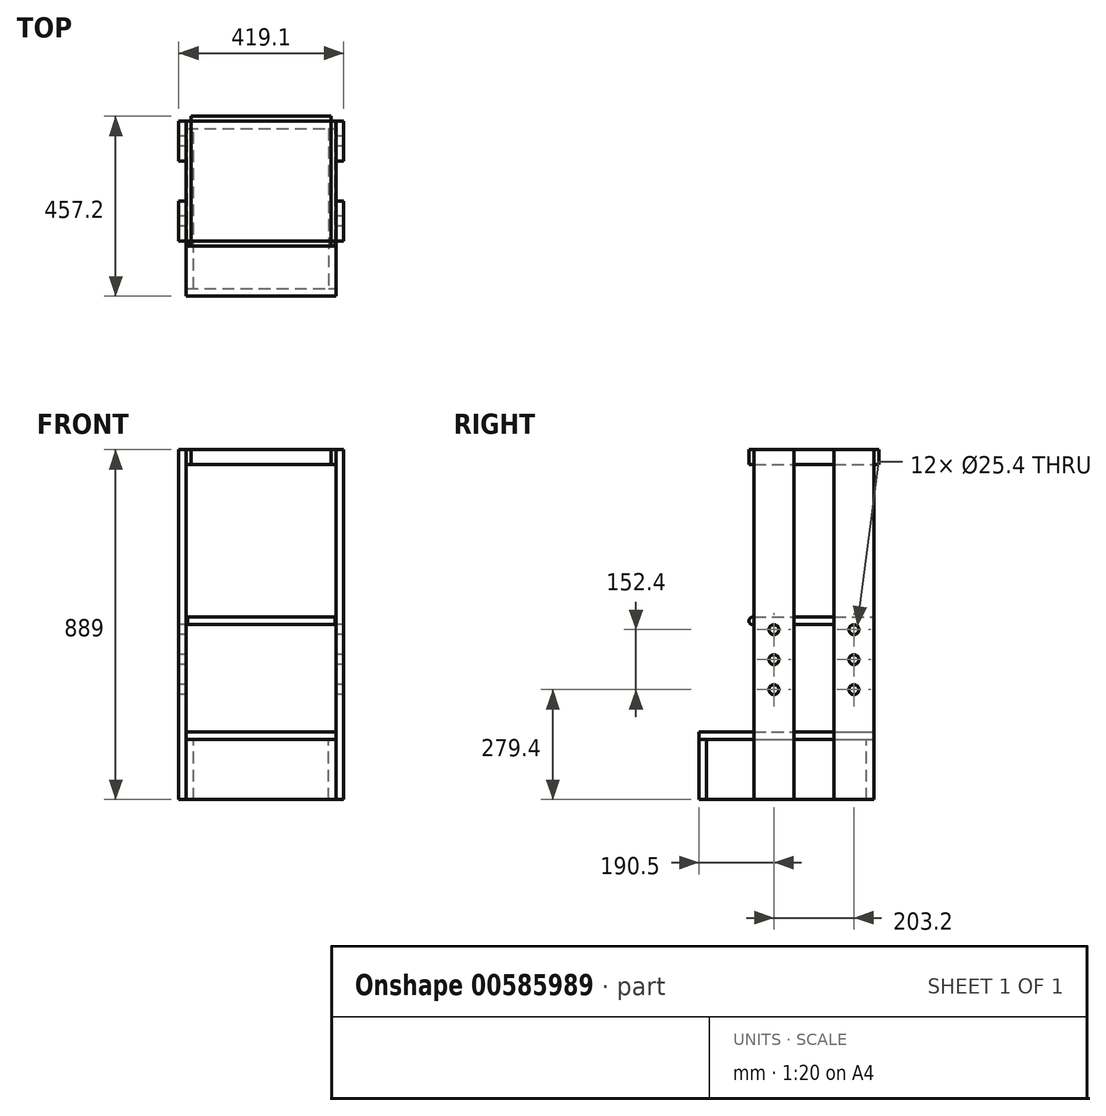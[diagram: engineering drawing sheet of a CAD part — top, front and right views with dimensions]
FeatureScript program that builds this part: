
annotation { "Feature Type Name" : "Feature", "Feature Type Description" : "" }
export const myFeature = defineFeature(function(context is Context, id is Id, definition is map)
    precondition{}
    {
        {
            var Q0;
            Q0=qCreatedBy(makeId("Top.planeOp"),FACE);
            var sketch = newSketch(context, id + "F0", { "sketchPlane" : qUnion([Q0])});
            skLineSegment(sketch, "E0.bottom", {"start": v(190.5, -222.25) * mm, "end": v(-190.5, -222.25) * mm});
            skLineSegment(sketch, "E0.top", {"start": v(190.5, 222.25) * mm, "end": v(-190.5, 222.25) * mm});
            skLineSegment(sketch, "E0.left", {"start": v(190.5, -222.25) * mm, "end": v(190.5, 222.25) * mm});
            skLineSegment(sketch, "E0.right", {"start": v(-190.5, -222.25) * mm, "end": v(-190.5, 222.25) * mm});
            skPoint(sketch, "E0.middle", {"position": v(0, 0) * mm});
            skSolve(sketch);
        }
        {
            var Q0;
            Q0=makeQuery(id+"F0.imprint","IMPRINT",FACE,{"disambiguationData":[TD([[makeQuery(id+"F0.imprint","IMPRINT",EDGE,{"derivedFrom":sQuery(id+"F0.wireOp",EDGE,"E0.bottom")}),-1.0]])]});
            var Q1;
            Q1=sQuery(id+"F0.wireOp",EDGE,"E0.right");
            extrude(context, id + "F1", {"entities" : qUnion([Q0]), "surfaceEntities" : qUnion([Q1]), "depth" : 19.05 * mm, "offsetDistance" : 25.4 * mm});
        }
        {
            var Q0;
            Q0=makeQuery(id+"F0.imprint","IMPRINT",FACE,{"disambiguationData":[TD([[makeQuery(id+"F0.imprint","IMPRINT",EDGE,{"derivedFrom":sQuery(id+"F0.wireOp",EDGE,"E0.bottom")}),-1.0]])]});
            var sketch = newSketch(context, id + "F2", { "sketchPlane" : qUnion([Q0])});
            skLineSegment(sketch, "E1.bottom", {"start": v(-190.5, 222.25) * mm, "end": v(190.5, 222.25) * mm});
            skLineSegment(sketch, "E1.top", {"start": v(-190.5, 203.2) * mm, "end": v(190.5, 203.2) * mm});
            skLineSegment(sketch, "E1.left", {"start": v(-190.5, 222.25) * mm, "end": v(-190.5, 203.2) * mm});
            skLineSegment(sketch, "E1.right", {"start": v(190.5, 222.25) * mm, "end": v(190.5, 203.2) * mm});
            skLineSegment(sketch, "E2.bottom", {"start": v(-190.5, -222.25) * mm, "end": v(190.5, -222.25) * mm});
            skLineSegment(sketch, "E2.top", {"start": v(-190.5, -203.2) * mm, "end": v(190.5, -203.2) * mm});
            skLineSegment(sketch, "E2.left", {"start": v(-190.5, -222.25) * mm, "end": v(-190.5, -203.2) * mm});
            skLineSegment(sketch, "E2.right", {"start": v(190.5, -222.25) * mm, "end": v(190.5, -203.2) * mm});
            skSolve(sketch);
        }
        {
            var Q0;
            Q0=makeQuery(id+"F2.imprint","IMPRINT",FACE,{"disambiguationData":[TD([[makeQuery(id+"F2.imprint","IMPRINT",EDGE,{"derivedFrom":sQuery(id+"F2.wireOp",EDGE,"E1.bottom")}),1.0]])]});
            var Q1;
            Q1=makeQuery(id+"F2.imprint","IMPRINT",FACE,{"disambiguationData":[TD([[makeQuery(id+"F2.imprint","IMPRINT",EDGE,{"derivedFrom":sQuery(id+"F2.wireOp",EDGE,"E2.bottom")}),-1.0]])]});
            extrude(context, id + "F3", {"entities" : qUnion([Q0, Q1]), "oppositeDirection" : true, "depth" : 152.4 * mm, "offsetDistance" : 25.4 * mm});
        }
        {
            var Q0;
            Q0=makeQuery(id+"F0.imprint","IMPRINT",FACE,{"disambiguationData":[TD([[makeQuery(id+"F0.imprint","IMPRINT",EDGE,{"derivedFrom":sQuery(id+"F0.wireOp",EDGE,"E0.bottom")}),-1.0]])]});
            var sketch = newSketch(context, id + "F4", { "sketchPlane" : qUnion([Q0])});
            skLineSegment(sketch, "E3.bottom", {"start": v(-190.5, -203.2) * mm, "end": v(-171.45, -203.2) * mm});
            skLineSegment(sketch, "E3.top", {"start": v(-190.5, 203.2) * mm, "end": v(-171.45, 203.2) * mm});
            skLineSegment(sketch, "E3.left", {"start": v(-190.5, -203.2) * mm, "end": v(-190.5, 203.2) * mm});
            skLineSegment(sketch, "E3.right", {"start": v(-171.45, -203.2) * mm, "end": v(-171.45, 203.2) * mm});
            skLineSegment(sketch, "E4.bottom", {"start": v(171.45, 203.2) * mm, "end": v(190.5, 203.2) * mm});
            skLineSegment(sketch, "E4.top", {"start": v(171.45, -203.2) * mm, "end": v(190.5, -203.2) * mm});
            skLineSegment(sketch, "E4.left", {"start": v(171.45, 203.2) * mm, "end": v(171.45, -203.2) * mm});
            skLineSegment(sketch, "E4.right", {"start": v(190.5, 203.2) * mm, "end": v(190.5, -203.2) * mm});
            skSolve(sketch);
        }
        {
            var Q0;
            Q0 = qSketchRegion(id + "F4", true);
            extrude(context, id + "F5", {"entities" : qUnion([Q0]), "oppositeDirection" : true, "depth" : 152.4 * mm, "offsetDistance" : 25.4 * mm});
        }
        {
            var Q0;
            Q0=makeQuery(id+"F5.opExtrude","SWEPT_FACE",FACE,{"disambiguationData":[OSD([sQuery(id+"F4.wireOp",EDGE,"E3.left")])]});
            var sketch = newSketch(context, id + "F6", { "sketchPlane" : qUnion([Q0])});
            skLineSegment(sketch, "E5.bottom", {"start": v(-222.25, -152.4) * mm, "end": v(-120.65, -152.4) * mm});
            skLineSegment(sketch, "E5.top", {"start": v(-222.25, 736.6) * mm, "end": v(-120.65, 736.6) * mm});
            skLineSegment(sketch, "E5.left", {"start": v(-222.25, -152.4) * mm, "end": v(-222.25, 736.6) * mm});
            skLineSegment(sketch, "E5.right", {"start": v(-120.65, -152.4) * mm, "end": v(-120.65, 736.6) * mm});
            skLineSegment(sketch, "E6.bottom", {"start": v(-19.05, -152.4) * mm, "end": v(82.55, -152.4) * mm});
            skLineSegment(sketch, "E6.top", {"start": v(-19.05, 736.6) * mm, "end": v(82.55, 736.6) * mm});
            skLineSegment(sketch, "E6.left", {"start": v(-19.05, -152.4) * mm, "end": v(-19.05, 736.6) * mm});
            skLineSegment(sketch, "E6.right", {"start": v(82.55, -152.4) * mm, "end": v(82.55, 736.6) * mm});
            skSolve(sketch);
        }
        {
            var Q0;
            Q0 = qSketchRegion(id + "F6", true);
            extrude(context, id + "F7", {"entities" : qUnion([Q0]), "depth" : 19.05 * mm, "offsetDistance" : 25.4 * mm});
        }
        {
            var Q0;
            Q0=makeQuery(id+"F7.opExtrude","SWEPT_BODY",BODY,{"disambiguationData":[OSD([sQuery(id+"F6.wireOp",EDGE,"E6.bottom"),sQuery(id+"F6.wireOp",EDGE,"E6.top"),sQuery(id+"F6.wireOp",EDGE,"E6.left"),sQuery(id+"F6.wireOp",EDGE,"E6.right")])]});
            var Q1;
            Q1=makeQuery(id+"F7.opExtrude","SWEPT_BODY",BODY,{"disambiguationData":[OSD([sQuery(id+"F6.wireOp",EDGE,"E5.bottom"),sQuery(id+"F6.wireOp",EDGE,"E5.top"),sQuery(id+"F6.wireOp",EDGE,"E5.left"),sQuery(id+"F6.wireOp",EDGE,"E5.right")])]});
            var Q2;
            Q2=qCreatedBy(makeId("Right.planeOp"),FACE);
            mirror(context, id + "F8", {"entities" : qUnion([Q0, Q1]), "mirrorPlane" : qUnion([Q2])});
        }
        {
            var Q0;
            Q0=makeQuery(id+"F7.opExtrude","CAP_FACE",FACE,{"disambiguationData":[OSD([sQuery(id+"F6.wireOp",EDGE,"E5.bottom"),sQuery(id+"F6.wireOp",EDGE,"E5.top"),sQuery(id+"F6.wireOp",EDGE,"E5.left"),sQuery(id+"F6.wireOp",EDGE,"E5.right")])],"isStart":false});
            var sketch = newSketch(context, id + "F9", { "sketchPlane" : qUnion([Q0])});
            skLineSegment(sketch, "E7", {"start": v(-171.45, 736.6) * mm, "end": v(-171.45, -152.4) * mm, "construction": true});
            skLineSegment(sketch, "E8", {"start": v(31.75, 736.6) * mm, "end": v(31.75, -152.4) * mm, "construction": true});
            skCircle(sketch, "E9", {"center": v(-171.45, 279.4) * mm, "radius": 12.7 * mm});
            skCircle(sketch, "E10", {"center": v(-171.45, 203.2) * mm, "radius": 12.7 * mm});
            skCircle(sketch, "E11", {"center": v(-171.45, 127) * mm, "radius": 12.7 * mm});
            skCircle(sketch, "E12", {"center": v(31.75, 127) * mm, "radius": 12.7 * mm});
            skCircle(sketch, "E13", {"center": v(31.75, 203.2) * mm, "radius": 12.7 * mm});
            skCircle(sketch, "E14", {"center": v(31.75, 279.4) * mm, "radius": 12.7 * mm});
            skLineSegment(sketch, "E15", {"start": v(-171.45, 292.1) * mm, "end": v(31.75, 292.1) * mm, "construction": true});
            skLineSegment(sketch, "E16", {"start": v(31.75, 292.1) * mm, "end": v(31.75, 215.9) * mm, "construction": true});
            skLineSegment(sketch, "E17", {"start": v(31.75, 215.9) * mm, "end": v(-171.45, 215.9) * mm, "construction": true});
            skLineSegment(sketch, "E18", {"start": v(-171.45, 215.9) * mm, "end": v(-171.45, 139.7) * mm, "construction": true});
            skLineSegment(sketch, "E19", {"start": v(-171.45, 139.7) * mm, "end": v(31.75, 139.7) * mm, "construction": true});
            skSolve(sketch);
        }
        {
            var Q0;
            Q0=sQuery(id+"F9.wireOp",VERTEX,"E9.center");
            var Q1;
            Q1=sQuery(id+"F9.wireOp",VERTEX,"E14.center");
            var Q2;
            Q2=sQuery(id+"F9.wireOp",VERTEX,"E13.center");
            var Q3;
            Q3=sQuery(id+"F9.wireOp",VERTEX,"E10.center");
            var Q4;
            Q4=sQuery(id+"F9.wireOp",VERTEX,"E11.center");
            var Q5;
            Q5=sQuery(id+"F9.wireOp",VERTEX,"E12.center");
            var Q6;
            Q6=makeQuery(id+"F7.opExtrude","SWEPT_BODY",BODY,{"disambiguationData":[OSD([sQuery(id+"F6.wireOp",EDGE,"E6.bottom"),sQuery(id+"F6.wireOp",EDGE,"E6.top"),sQuery(id+"F6.wireOp",EDGE,"E6.left"),sQuery(id+"F6.wireOp",EDGE,"E6.right")])]});
            var Q7;
            Q7=makeQuery(id+"F7.opExtrude","SWEPT_BODY",BODY,{"disambiguationData":[OSD([sQuery(id+"F6.wireOp",EDGE,"E5.bottom"),sQuery(id+"F6.wireOp",EDGE,"E5.top"),sQuery(id+"F6.wireOp",EDGE,"E5.left"),sQuery(id+"F6.wireOp",EDGE,"E5.right")])]});
            var Q8;
            Q8=makeQuery(id+"F8.opPattern","COPY",BODY,{"derivedFrom":makeQuery(id+"F7.opExtrude","SWEPT_BODY",BODY,{"disambiguationData":[OSD([sQuery(id+"F6.wireOp",EDGE,"E5.bottom"),sQuery(id+"F6.wireOp",EDGE,"E5.top"),sQuery(id+"F6.wireOp",EDGE,"E5.left"),sQuery(id+"F6.wireOp",EDGE,"E5.right")])]}),"instanceName":"1"});
            var Q9;
            Q9=makeQuery(id+"F8.opPattern","COPY",BODY,{"derivedFrom":makeQuery(id+"F7.opExtrude","SWEPT_BODY",BODY,{"disambiguationData":[OSD([sQuery(id+"F6.wireOp",EDGE,"E6.bottom"),sQuery(id+"F6.wireOp",EDGE,"E6.top"),sQuery(id+"F6.wireOp",EDGE,"E6.left"),sQuery(id+"F6.wireOp",EDGE,"E6.right")])]}),"instanceName":"1"});
            hole(context, id + "F10", {"style" : HoleStyle.SIMPLE, "endStyle" : HoleEndStyle.THROUGH, "holeDiameter" : 25.4 * mm, "majorDiameter" : 6.35 * mm, "isTappedThrough" : true, "tappedDepth" : 12.7 * mm, "tapClearance" : 3, "locations" : qUnion([Q0, Q1, Q2, Q3, Q4, Q5]), "scope" : qUnion([Q6, Q7, Q8, Q9])});
        }
        {
            var Q0;
            Q0=sQuery(id+"F9.wireOp",EDGE,"E15");
            cPoint(context, id + "F11", {"entities" : qUnion([Q0]), "parameter" : 0.5});
        }
        {
            var Q0;
            Q0 = qCreatedBy(id + "F11" ,VERTEX);
            var Q1;
            Q1=qCreatedBy(makeId("Top.planeOp"),FACE);
            cPlane(context, id + "F12", {"entities" : qUnion([Q0, Q1]), "cplaneType" : CPlaneType.PLANE_POINT, "offset" : 304.8 * mm, "width" : 152.4 * mm, "height" : 152.4 * mm});
        }
        {
            var Q0;
            Q0=qCreatedBy(id+"F12.planeOp",FACE);
            var sketch = newSketch(context, id + "F13", { "sketchPlane" : qUnion([Q0])});
            skLineSegment(sketch, "E20.bottom", {"start": v(187.32, -95.25) * mm, "end": v(-187.32, -95.25) * mm});
            skLineSegment(sketch, "E20.top", {"start": v(187.33, 222.25) * mm, "end": v(-187.33, 222.25) * mm});
            skLineSegment(sketch, "E20.left", {"start": v(187.33, -26.1) * mm, "end": v(187.33, 222.25) * mm});
            skLineSegment(sketch, "E20.right", {"start": v(-187.32, -82.55) * mm, "end": v(-187.32, 222.25) * mm});
            skPoint(sketch, "E20.middle", {"position": v(0, 69.85) * mm});
            skLineSegment(sketch, "E21", {"start": v(-187.32, -95.25) * mm, "end": v(-187.32, -82.55) * mm});
            skLineSegment(sketch, "E22", {"start": v(187.33, -95.25) * mm, "end": v(187.33, -26.1) * mm});
            skPoint(sketch, "E23", {"position": v(0, 222.25) * mm});
            skSolve(sketch);
        }
        {
            var Q0;
            Q0 = qSketchRegion(id + "F13", true);
            extrude(context, id + "F14", {"entities" : qUnion([Q0]), "depth" : 19.05 * mm, "offsetDistance" : 25.4 * mm});
        }
        {
            var Q0;
            Q0=makeQuery(id+"F7.opExtrude","CAP_FACE",FACE,{"disambiguationData":[OSD([sQuery(id+"F6.wireOp",EDGE,"E6.bottom"),sQuery(id+"F6.wireOp",EDGE,"E6.top"),sQuery(id+"F6.wireOp",EDGE,"E6.left"),sQuery(id+"F6.wireOp",EDGE,"E6.right")])],"isStart":true});
            var sketch = newSketch(context, id + "F15", { "sketchPlane" : qUnion([Q0])});
            skLineSegment(sketch, "E24.bottom", {"start": v(-82.55, 736.6) * mm, "end": v(222.25, 736.6) * mm});
            skLineSegment(sketch, "E24.top", {"start": v(-82.55, 698.5) * mm, "end": v(222.25, 698.5) * mm});
            skLineSegment(sketch, "E24.left", {"start": v(-82.55, 736.6) * mm, "end": v(-82.55, 698.5) * mm});
            skLineSegment(sketch, "E24.right", {"start": v(222.25, 736.6) * mm, "end": v(222.25, 698.5) * mm});
            skSolve(sketch);
        }
        {
            var Q0;
            Q0 = qSketchRegion(id + "F15", true);
            extrude(context, id + "F16", {"entities" : qUnion([Q0]), "depth" : 12.7 * mm, "offsetDistance" : 25.4 * mm});
        }
        {
            var Q0;
            Q0=makeQuery(id+"F16.opExtrude","SWEPT_BODY",BODY,{"disambiguationData":[OSD([sQuery(id+"F15.wireOp",EDGE,"E24.bottom"),sQuery(id+"F15.wireOp",EDGE,"E24.top"),sQuery(id+"F15.wireOp",EDGE,"E24.left"),sQuery(id+"F15.wireOp",EDGE,"E24.right")])]});
            var Q1;
            Q1=qCreatedBy(makeId("Right.planeOp"),FACE);
            mirror(context, id + "F17", {"entities" : qUnion([Q0]), "mirrorPlane" : qUnion([Q1])});
        }
        {
            var Q0;
            Q0=makeQuery(id+"F7.opExtrude","SWEPT_FACE",FACE,{"disambiguationData":[OSD([sQuery(id+"F6.wireOp",EDGE,"E6.right")])]});
            var sketch = newSketch(context, id + "F18", { "sketchPlane" : qUnion([Q0])});
            skLineSegment(sketch, "E25.bottom", {"start": v(-177.8, 736.6) * mm, "end": v(177.8, 736.6) * mm});
            skLineSegment(sketch, "E25.top", {"start": v(-177.8, 698.5) * mm, "end": v(177.8, 698.5) * mm});
            skLineSegment(sketch, "E25.left", {"start": v(177.8, 736.6) * mm, "end": v(177.8, 698.5) * mm});
            skLineSegment(sketch, "E25.right", {"start": v(-177.8, 736.6) * mm, "end": v(-177.8, 698.5) * mm});
            skSolve(sketch);
        }
        {
            var Q0;
            Q0 = qSketchRegion(id + "F18", true);
            extrude(context, id + "F19", {"entities" : qUnion([Q0]), "depth" : 12.7 * mm, "offsetDistance" : 25.4 * mm});
        }
        {
            var Q0;
            Q0=makeQuery(id+"F17.opPattern","COPY",EDGE,{"derivedFrom":makeQuery(id+"F16.opExtrude","CAP_EDGE",EDGE,{"disambiguationData":[OSD([sQuery(id+"F15.wireOp",EDGE,"E24.top")])],"isStart":false}),"instanceName":"1"});
            cPoint(context, id + "F20", {"entities" : qUnion([Q0]), "parameter" : 0.5});
        }
        {
            var Q0;
            Q0=qCreatedBy(makeId("Front.planeOp"),FACE);
            var Q1;
            Q1 = qCreatedBy(id + "F20" ,VERTEX);
            cPlane(context, id + "F21", {"entities" : qUnion([Q0, Q1]), "cplaneType" : CPlaneType.PLANE_POINT, "offset" : 25.4 * mm, "width" : 152.4 * mm, "height" : 152.4 * mm});
        }
        {
            var Q0;
            Q0=makeQuery(id+"F19.opExtrude","SWEPT_BODY",BODY,{"disambiguationData":[OSD([sQuery(id+"F18.wireOp",EDGE,"E25.bottom"),sQuery(id+"F18.wireOp",EDGE,"E25.top"),sQuery(id+"F18.wireOp",EDGE,"E25.left"),sQuery(id+"F18.wireOp",EDGE,"E25.right")])]});
            var Q1;
            Q1=qCreatedBy(id+"F21.planeOp",FACE);
            mirror(context, id + "F22", {"entities" : qUnion([Q0]), "mirrorPlane" : qUnion([Q1])});
        }
        {
            var Q0;
            Q0=makeQuery(id+"F14.opExtrude","CAP_EDGE",EDGE,{"disambiguationData":[OSD([sQuery(id+"F13.wireOp",EDGE,"E20.bottom")])],"isStart":false});
            var Q1;
            Q1=makeQuery(id+"F14.opExtrude","CAP_EDGE",EDGE,{"disambiguationData":[OSD([sQuery(id+"F13.wireOp",EDGE,"E20.bottom")])],"isStart":true});
            fillet(context, id + "F23", {"entities" : qUnion([Q0, Q1]), "radius" : 9.52 * mm, "tangentPropagation" : true, "allowEdgeOverflow" : false});
        }
    });
